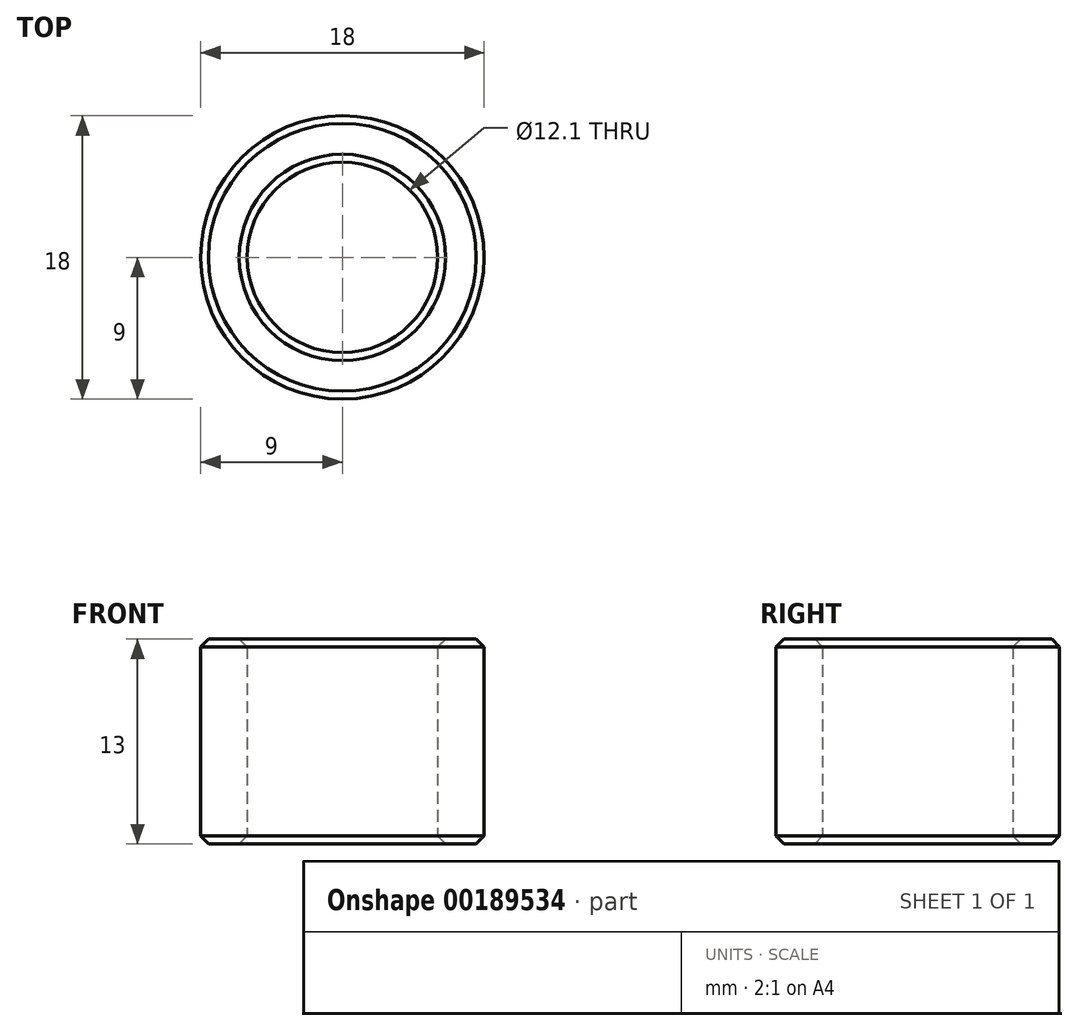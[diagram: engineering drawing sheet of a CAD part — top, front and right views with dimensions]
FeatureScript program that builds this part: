
annotation { "Feature Type Name" : "Feature", "Feature Type Description" : "" }
export const myFeature = defineFeature(function(context is Context, id is Id, definition is map)
    precondition{}
    {
        {
            var Q0;
            Q0=qCreatedBy(makeId("Top.planeOp"),FACE);
            var sketch = newSketch(context, id + "F0", { "sketchPlane" : qUnion([Q0])});
            skCircle(sketch, "E0", {"center": v(0, 0) * mm, "radius": 9 * mm});
            skCircle(sketch, "E1", {"center": v(0, 0) * mm, "radius": 6.05 * mm});
            skSolve(sketch);
        }
        {
            var Q0;
            Q0=makeQuery(id+"F0.imprint","IMPRINT",FACE,{"disambiguationData":[TD([[makeQuery(id+"F0.imprint","IMPRINT",EDGE,{"derivedFrom":sQuery(id+"F0.wireOp",EDGE,"E0")}),1.0]])]});
            extrude(context, id + "F1", {"entities" : qUnion([Q0]), "depth" : 13 * mm});
        }
        {
            var Q0;
            Q0=makeQuery(id+"F1.opExtrude","SWEPT_FACE",FACE,{"disambiguationData":[OSD([sQuery(id+"F0.wireOp",EDGE,"E1")])]});
            var Q1;
            Q1=makeQuery(id+"F1.opExtrude","SWEPT_FACE",FACE,{"disambiguationData":[OSD([sQuery(id+"F0.wireOp",EDGE,"E0")])]});
            chamfer(context, id + "F2", {"entities" : qUnion([Q0, Q1]), "width" : 0.5 * mm, "tangentPropagation" : true});
        }
    });
